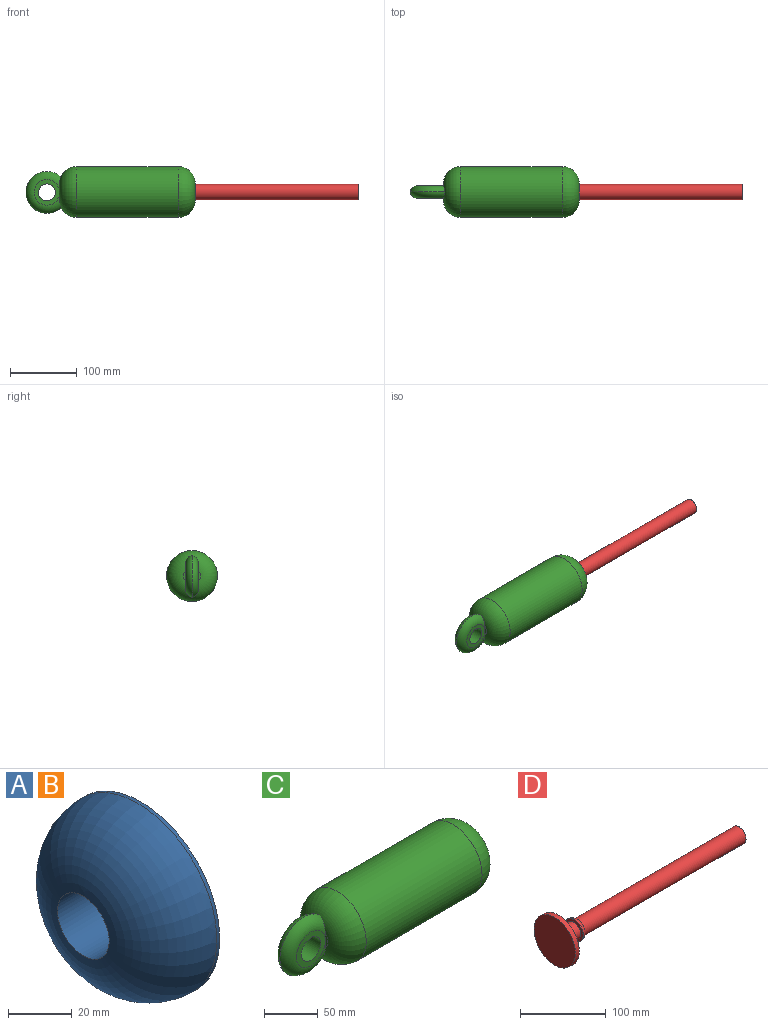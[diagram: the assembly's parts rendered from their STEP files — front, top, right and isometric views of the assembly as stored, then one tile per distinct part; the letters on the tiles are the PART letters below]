
ASSEMBLY  parts=4 mates=4
PART A: 4 faces, bbox 25.4x69.9x69.9 mm
  f0: plane 69.85x69.85mm, normal (1,0,0), area 3421.5mm2, adj f1,f3
  f1: cylinder r=34.92mm len=69.85mm, axis (-1,0,0), area 278.7mm2, adj f0,f2
  f2: torus R=10.79mm, axis (-1,0,0), area 6185mm2, adj f1,f3
  f3: cylinder r=11.43mm len=25.39mm, axis (1,0,0), area 1823.5mm2, adj f0,f2
PART B: same geometry as A
PART C: 21 faces, bbox 256.4x76.2x76.2 mm
  f0: plane 17.04x3.32mm, normal (-1,0,0), area 36.9mm2, adj f3,f7,f9
  f1: plane 17.04x3.32mm, normal (-1,0,0), area 36.9mm2, adj f3,f6,f8
  f2: cylinder r=38.1mm len=152.4mm, axis (-1,0,0), area 36482.9mm2, adj f3,f4
  f3: torus R=12.7mm, axis (-1,0,0), area 6920.9mm2, adj f0,f1,f2,f8,f9
  f4: torus R=12.7mm, axis (-1,0,0), area 7237.4mm2, adj f2,f10
  f5: cylinder r=12.7mm len=25.4mm, axis (0,1,0), area 1520.1mm2, adj f6,f7
  f6: plane 38.1x37.89mm, normal (0,-1,0), area 632.6mm2, adj f1,f5,f8
  f7: plane 38.1x37.89mm, normal (0,1,0), area 632.6mm2, adj f0,f5,f9
  f8: torus R=19.05mm, axis (0,-1,0), area 2144.8mm2, adj f1,f3,f6,f9
  f9: torus R=19.05mm, axis (0,-1,0), area 2144.8mm2, adj f0,f3,f7,f8
  f10: cylinder r=12.7mm len=25.4mm, axis (-1,0,0), area 243.2mm2, adj f4,f15
  f11: plane 23.76x8.47mm, normal (1,0,0), area 115.2mm2, adj f14,f20
  f12: plane 23.76x8.47mm, normal (1,0,0), area 115.2mm2, adj f14,f19
  f13: cylinder r=35.05mm len=152.4mm, axis (-1,0,0), area 33564.3mm2, adj f14,f15
  f14: torus R=12.7mm, axis (-1,0,0), area 5889.6mm2, adj f11,f12,f13,f19,f20
  f15: torus R=12.7mm, axis (-1,0,0), area 5940.8mm2, adj f10,f13
  f16: cylinder r=15.75mm len=31.5mm, axis (0,1,0), area 1281.8mm2, adj f17,f18
  f17: plane 38.1x38.1mm, normal (0,1,0), area 361mm2, adj f16,f19
  f18: plane 38.1x38.1mm, normal (0,-1,0), area 361mm2, adj f16,f20
  f19: torus R=19.05mm, axis (0,-1,0), area 1583.9mm2, adj f12,f14,f17,f20
  f20: torus R=19.05mm, axis (0,-1,0), area 1583.9mm2, adj f11,f14,f18,f19
PART D: 9 faces, bbox 304.8x68.6x68.6 mm
  f0: plane 30.13x30.13mm, normal (-1,0,0), area 302.6mm2, adj f1,f7
  f1: cylinder r=11.43mm len=25.4mm, axis (-1,0,0), area 1824.1mm2, adj f0,f2
  f2: plane 68.58x68.58mm, normal (1,0,0), area 3283.5mm2, adj f1,f3
  f3: cylinder r=34.29mm len=68.58mm, axis (-1,0,0), area 1368.1mm2, adj f2,f4
  f4: plane 68.58x68.58mm, normal (-1,0,0), area 3693.9mm2, adj f3
  f5: plane 22.86x22.86mm, normal (1,0,0), area 410.4mm2, adj f6
  f6: cylinder r=11.43mm len=266.7mm, axis (-1,0,0), area 19153.5mm2, adj f5,f8
  f7: cylinder r=15.07mm len=30.13mm, axis (-1,0,0), area 57.7mm2, adj f0,f8
  f8: torus R=8.72mm, axis (1,0,0), area 621.6mm2, adj f6,f7
PLACE A rot(axis=(0,-0.65,0.76),180deg) t=(72.3,0,0)mm
PLACE B rot(axis=(1,0,0),180deg) t=(-98.81,0,0)mm
PLACE C t=(1.47,0,0)mm
PLACE D rot(axis=(-1,0,0),99.6deg) t=(40.55,0,0)mm
MATE cylindrical C.f2 <-> B.f1  axis (-1,0,0) through (-94.16,0,0)mm
MATE cylindrical A.f1 <-> C.f2  axis (1,0,0) through (48.17,0,0)mm
MATE fastened D.f1 <-> A.f1  axis (1,0,0) through (46.9,0,0)mm
MATE cylindrical D.f1 <-> C.f2  axis (-1,0,0) through (40.55,0,0)mm
